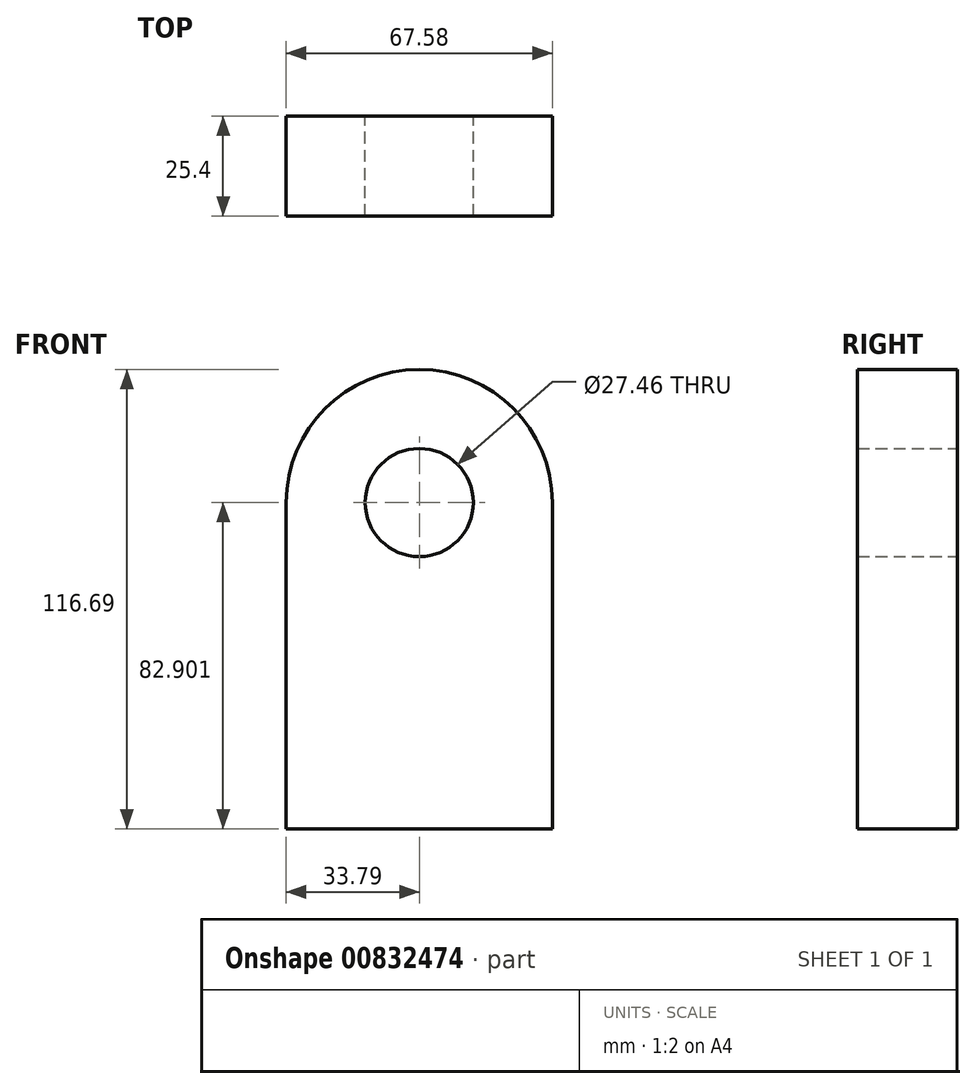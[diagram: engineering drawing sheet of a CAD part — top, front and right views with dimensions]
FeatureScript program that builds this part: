
annotation { "Feature Type Name" : "Feature", "Feature Type Description" : "" }
export const myFeature = defineFeature(function(context is Context, id is Id, definition is map)
    precondition{}
    {
        {
            var Q0;
            Q0=qCreatedBy(makeId("Front.planeOp"),FACE);
            var sketch = newSketch(context, id + "F0", { "sketchPlane" : qUnion([Q0])});
            skLineSegment(sketch, "E0.bottom", {"start": v(33.79, -39.8) * mm, "end": v(-33.79, -39.8) * mm});
            skLineSegment(sketch, "E0.left", {"start": v(33.79, -39.8) * mm, "end": v(33.79, 43.1) * mm});
            skLineSegment(sketch, "E0.right", {"start": v(-33.79, -39.8) * mm, "end": v(-33.79, 43.1) * mm});
            skArc(sketch, "E1", {"start": v(33.79, 43.1) * mm, "mid": v(0, 76.88) * mm, "end": v(-33.79, 43.1) * mm});
            skCircle(sketch, "E2", {"center": v(0, 43.1) * mm, "radius": 13.73 * mm});
            skSolve(sketch);
        }
        {
            var Q0;
            Q0 = qSketchRegion(id + "F0", true);
            extrude(context, id + "F1", {"entities" : qUnion([Q0]), "depth" : 25.4 * mm, "offsetDistance" : 25.4 * mm});
        }
    });
